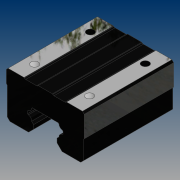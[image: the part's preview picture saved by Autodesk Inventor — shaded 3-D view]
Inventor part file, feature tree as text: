
AUTODESK INVENTOR PART (.ipt)
format: ipt  version: 2021 (Build 250183000, 183)  size: 180,224 bytes
history: native  units: mm
features: extrude x2, sketch x2, projected_geometry x2
ambient origin geometry x8: Origin, YZ Plane, XZ Plane, XY Plane, X Axis, Y Axis, Z Axis, Center Point
bodies: Solid1 (feature_tree)
feature tree (6):
  extrude  "Extrusion1"  Depth=6.0mm TaperAngle=0.0deg
  extrude  "Extrusion2"  Depth=4.2mm
  sketch  "Sketch1"  dims[d0=50.5mm d1=0.0mm d2=6.0mm d3=0.0mm]
  sketch  "Sketch3"  dims[d5=31.0mm d6=4.2mm d7=15.75mm]
  projected_geometry  "Projected Loop1"
  projected_geometry  "Projected Loop2"
